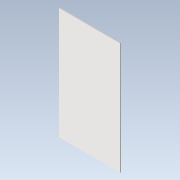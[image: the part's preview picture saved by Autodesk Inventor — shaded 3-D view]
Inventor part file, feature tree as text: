
AUTODESK INVENTOR PART (.ipt)
format: ipt  version: 2021 (Build 250183000, 183)  size: 83,968 bytes
history: native  units: mm
features: other x1, extrude x1, fillet x1, sketch x1
ambient origin geometry x8: Origin, YZ Plane, XZ Plane, XY Plane, X Axis, Y Axis, Z Axis, Center Point
bodies: Body1 (feature_tree)
feature tree (4):
  other  "Sólido1"
  extrude  "Extrusión1"  Depth=120.0mm
  fillet  "Empalme1"  Radius=50.0mm
  sketch  "Boceto1"  dims[d0=1.0mm d1=0.0mm d2=120.0mm d3=50.0mm d4=2.0mm]
